# Revit family: Door-Operator_Electric_Tormax_iMotion-TN-110
name_source: partatom
category: Specialty Equipment
units: mm (PartAtom-declared; Revit-internal decimal feet)

## family parameters
Classification Number = 23.30.40.11.34
Cut with Voids When Loaded = No
Enable Cutting in Views = No
Host = Face
Maintain Annotation Orientation = No
Part Type = Normal
Room Calculation Point = No
Round Connector Dimension = Use Diameter
Shared = No

## types (2) — shared parameters
Assembly Code = C1020410
Available Options = as Specified
Box Length = 1' - 5 11/16"
Box Width = 0' - 11 17/32"
Capacity = Up to 1000 lbs or up to 72 inch Wide Panels
Construction Details = https://www.arcat.com
Default Elevation = 0' - 0"
Description = Tormax In-Floor Swing Door Operator - iMotion TN 110 as Specified
Electrical Notes = Controller to Operator is LV
Green Building-LEED = https://www.arcat.com
Keynote = 08 71 13
Manufacturer = TORMAX USA Inc.
Manufacturer Fax = 210-494-5930
Manufacturer Website = http://www.tormaxusa.com
Product Data = https://www.arcat.com
Revision = R1_2018-04
Rough Length = 1' - 7 3/4"
Rough Width = 1' - 5 3/4"
Sales Information = http://www.tormaxusa.com
Sound Pressure = <70 dBA
SpecWizard = https://www.arcat.com
Specification = https://www.arcat.com
Standards Conformance = NEMA 6 Case  ;  ANSI A156.10 and A156.19  ;  ADA
URL = http://www.tormaxusa.com
zero-valued in all types: Expected Lifespan (Years), Maintenance Schedule (Months), Warranty Duration (Years)

## per-type parameters (varying)
| type | Box Type | Conduit A Depth | Conduit B Depth | Conduit C Depth | Model | Rough Depth | Unit Depth | Unit Length | Unit Width |
| Surface Mount | iMotionTN110-Cover | 0' - 3 3/16" | 0' - 1 1/2" | 0' - 4" | iMotion TN 110 In-Floor Surface Mount | 0' - 5 1/2" | 0' - 5" | 1' - 6 15/16" | 1' - 0 5/8" |
| Flush | iMotionTN110-Flush | 0' - 5 3/16" | 0' - 2 7/8" | 0' - 5 3/8" | iMotion TN 110 In-Floor Flush | 0' - 6 7/8" | 0' - 6 3/8" | 1' - 5 11/16" | 1' - 1 1/4" |

## geometry (parser evidence)
native form markers: Sweep x7
no freeform markers — native parametric forms only
